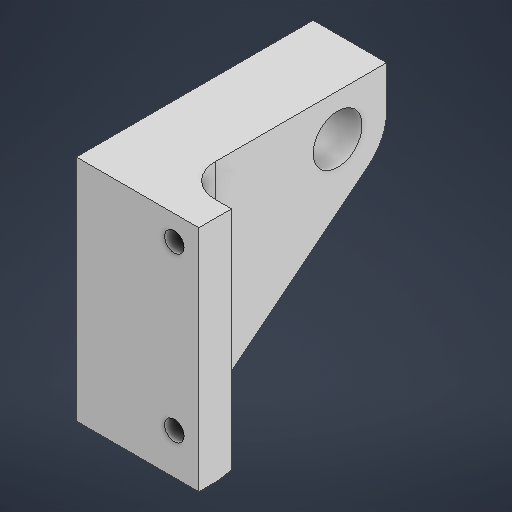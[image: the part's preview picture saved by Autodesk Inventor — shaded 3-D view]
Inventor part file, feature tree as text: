
AUTODESK INVENTOR PART (.ipt)
format: ipt  version: 2025 (Build 290162000, 162)  size: 205,312 bytes
history: native  units: mm
features: sketch x4, other x3
ambient origin geometry x8: Origin, YZ Plane, XZ Plane, XY Plane, X Axis, Y Axis, Z Axis, Center Point
bodies: 实体1 (feature_tree)
feature tree (7):
  other  "悬挂链.ipt"
  other  "实体1::悬挂链.ipt"
  other  "标记特征1"
  sketch  "草图1"  dims[d0=10.0mm]
  sketch  "草图2"
  sketch  "草图3"
  sketch  "草图4"
